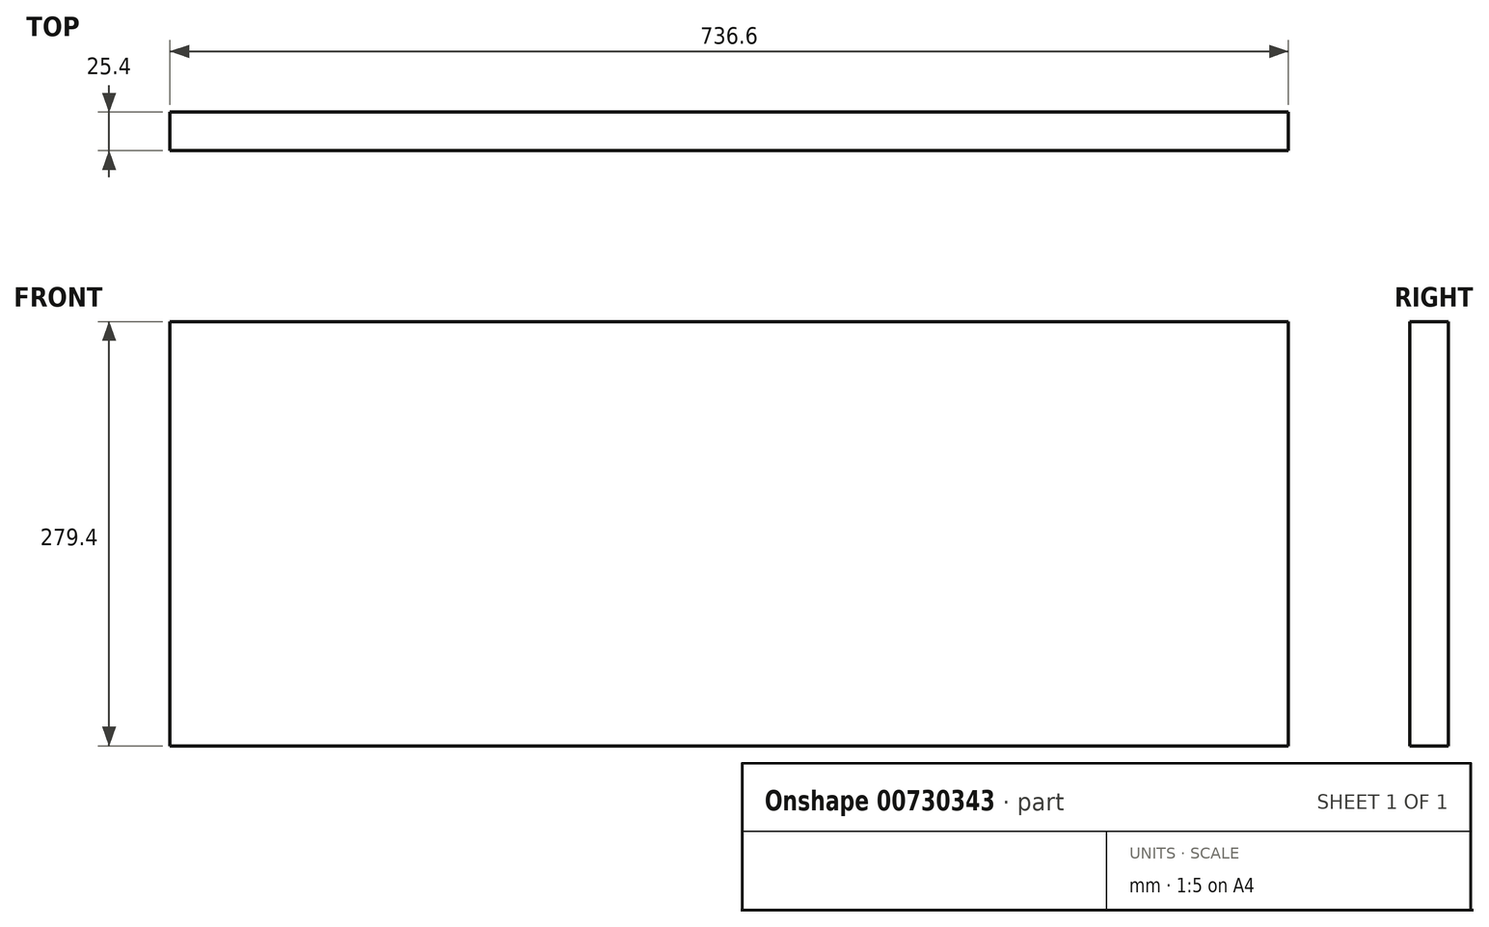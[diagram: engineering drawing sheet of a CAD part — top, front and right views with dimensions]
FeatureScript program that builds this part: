
annotation { "Feature Type Name" : "Feature", "Feature Type Description" : "" }
export const myFeature = defineFeature(function(context is Context, id is Id, definition is map)
    precondition{}
    {
        {
            var Q0;
            Q0=qCreatedBy(makeId("Top.planeOp"),FACE);
            var sketch = newSketch(context, id + "F0", { "sketchPlane" : qUnion([Q0])});
            skLineSegment(sketch, "E0.bottom", {"start": v(368.3, -12.7) * mm, "end": v(-368.3, -12.7) * mm});
            skLineSegment(sketch, "E0.top", {"start": v(368.3, 12.7) * mm, "end": v(-368.3, 12.7) * mm});
            skLineSegment(sketch, "E0.left", {"start": v(368.3, -12.7) * mm, "end": v(368.3, 12.7) * mm});
            skLineSegment(sketch, "E0.right", {"start": v(-368.3, -12.7) * mm, "end": v(-368.3, 12.7) * mm});
            skPoint(sketch, "E0.middle", {"position": v(0, 0) * mm});
            skSolve(sketch);
        }
        {
            var Q0;
            Q0=makeQuery(id+"F0.imprint","IMPRINT",FACE,{"disambiguationData":[TD([[makeQuery(id+"F0.imprint","IMPRINT",EDGE,{"derivedFrom":sQuery(id+"F0.wireOp",EDGE,"E0.bottom")}),-1.0]])]});
            extrude(context, id + "F1", {"entities" : qUnion([Q0]), "endBound" : BoundingType.SYMMETRIC, "oppositeDirection" : true, "depth" : 279.4 * mm, "offsetDistance" : 25.4 * mm});
        }
    });
